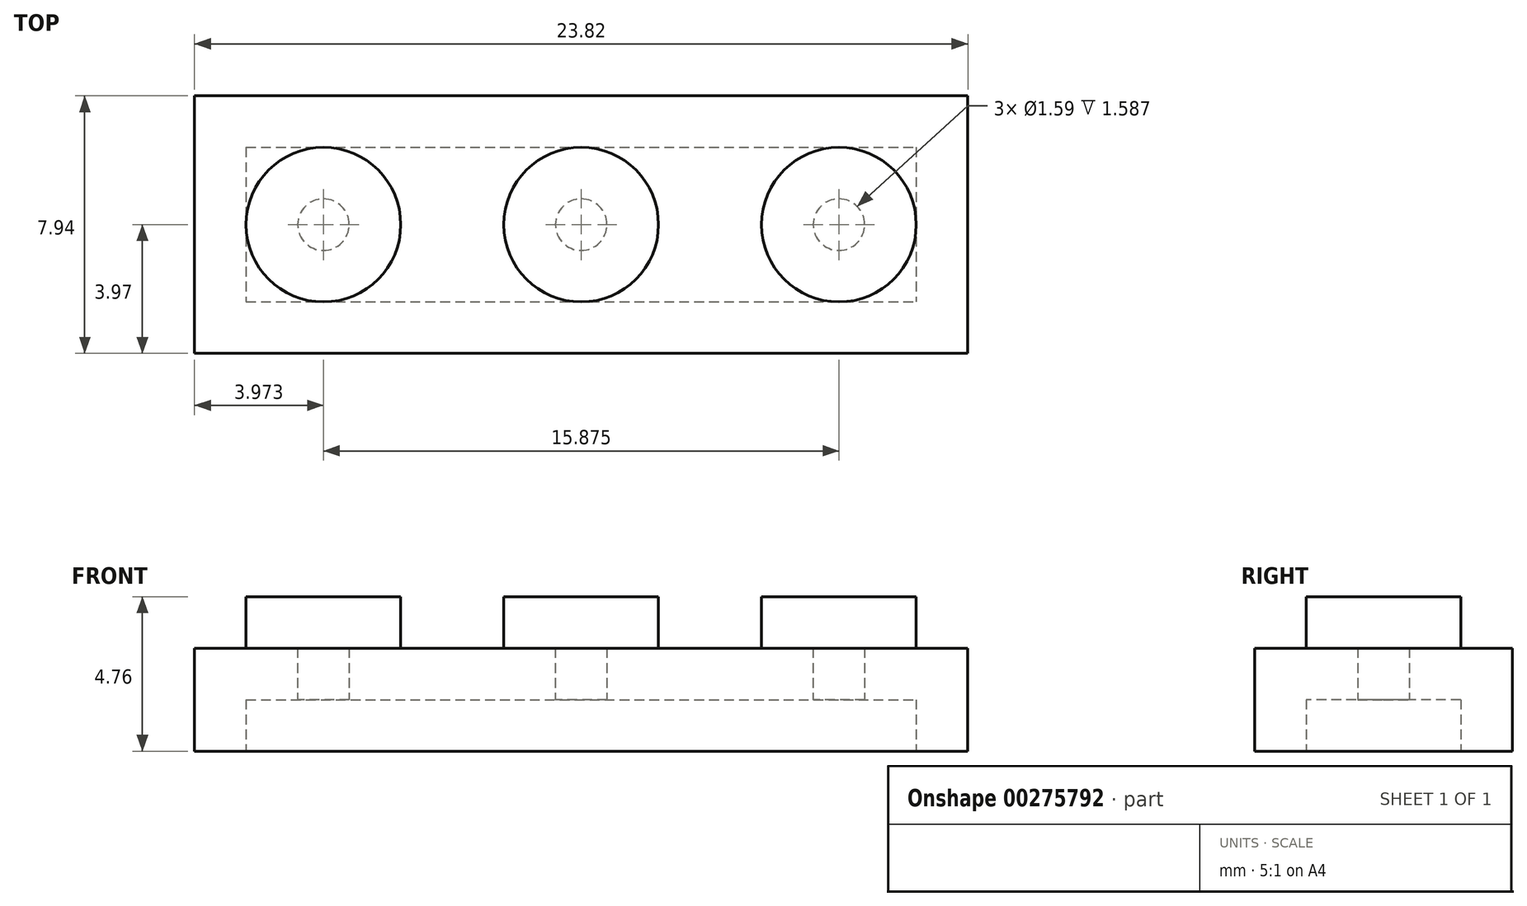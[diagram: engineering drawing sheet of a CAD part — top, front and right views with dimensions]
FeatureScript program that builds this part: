
annotation { "Feature Type Name" : "Feature", "Feature Type Description" : "" }
export const myFeature = defineFeature(function(context is Context, id is Id, definition is map)
    precondition{}
    {
        {
            var Q0;
            Q0=qCreatedBy(makeId("Top.planeOp"),FACE);
            var sketch = newSketch(context, id + "F0", { "sketchPlane" : qUnion([Q0])});
            skLineSegment(sketch, "E0.bottom", {"start": v(-11.9, 3.97) * mm, "end": v(11.9, 3.97) * mm});
            skLineSegment(sketch, "E0.top", {"start": v(-11.9, -3.97) * mm, "end": v(11.9, -3.97) * mm});
            skLineSegment(sketch, "E0.left", {"start": v(-11.9, 3.97) * mm, "end": v(-11.9, -3.97) * mm});
            skLineSegment(sketch, "E0.right", {"start": v(11.9, 3.97) * mm, "end": v(11.9, -3.97) * mm});
            skPoint(sketch, "E0.middle", {"position": v(0, 0) * mm});
            skCircle(sketch, "E1", {"center": v(-7.94, 0) * mm, "radius": 2.38 * mm});
            skCircle(sketch, "E2.1.0.0", {"center": v(0, 0) * mm, "radius": 2.38 * mm});
            skCircle(sketch, "E2.2.0.0", {"center": v(7.94, 0) * mm, "radius": 2.38 * mm});
            skLineSegment(sketch, "E2.direction1", {"start": v(-7.94, 0) * mm, "end": v(0, 0) * mm, "construction": true});
            skSolve(sketch);
        }
        {
            var Q0;
            Q0=qSketchRegion(id+"F0",true);
            extrude(context, id + "F1", {"entities" : qUnion([Q0]), "depth" : 3.17 * mm});
        }
        {
            var Q0;
            Q0=makeQuery(id+"F0.imprint","IMPRINT",FACE,{"disambiguationData":[TD([[makeQuery(id+"F0.imprint","IMPRINT",EDGE,{"derivedFrom":sQuery(id+"F0.wireOp",EDGE,"E1")}),1.0]])]});
            var Q1;
            Q1=makeQuery(id+"F0.imprint","IMPRINT",FACE,{"disambiguationData":[TD([[makeQuery(id+"F0.imprint","IMPRINT",EDGE,{"derivedFrom":sQuery(id+"F0.wireOp",EDGE,"E2.1.0.0")}),1.0]])]});
            var Q2;
            Q2=makeQuery(id+"F0.imprint","IMPRINT",FACE,{"disambiguationData":[TD([[makeQuery(id+"F0.imprint","IMPRINT",EDGE,{"derivedFrom":sQuery(id+"F0.wireOp",EDGE,"E2.2.0.0")}),1.0]])]});
            extrude(context, id + "F2", {"entities" : qUnion([Q0, Q1, Q2]), "operationType" : NewBodyOperationType.ADD, "depth" : 4.76 * mm});
        }
        {
            var Q0;
            {var subQ0=sQuery(id+"F0.wireOp",EDGE,"E2.2.0.0");var subQ1=sQuery(id+"F0.wireOp",EDGE,"E2.1.0.0");var subQ2=sQuery(id+"F0.wireOp",EDGE,"E1");Q0=makeQuery(id+"F2.boolean.opBoolean","MERGE",FACE,{"derivedFrom":[makeQuery(id+"F1.opExtrude","CAP_FACE",FACE,{"disambiguationData":[OSD([sQuery(id+"F0.wireOp",EDGE,"E0.bottom"),sQuery(id+"F0.wireOp",EDGE,"E0.top"),sQuery(id+"F0.wireOp",EDGE,"E0.left"),sQuery(id+"F0.wireOp",EDGE,"E0.right"),subQ2,subQ1,subQ0])],"isStart":true}),makeQuery(id+"F2.opExtrude","CAP_FACE",FACE,{"disambiguationData":[OSD([subQ2])],"isStart":true}),makeQuery(id+"F2.opExtrude","CAP_FACE",FACE,{"disambiguationData":[OSD([subQ1])],"isStart":true}),makeQuery(id+"F2.opExtrude","CAP_FACE",FACE,{"disambiguationData":[OSD([subQ0])],"isStart":true})]});}
            shell(context, id + "F3", {"entities" : qUnion([Q0]), "thickness" : 1.59 * mm});
        }
    });
